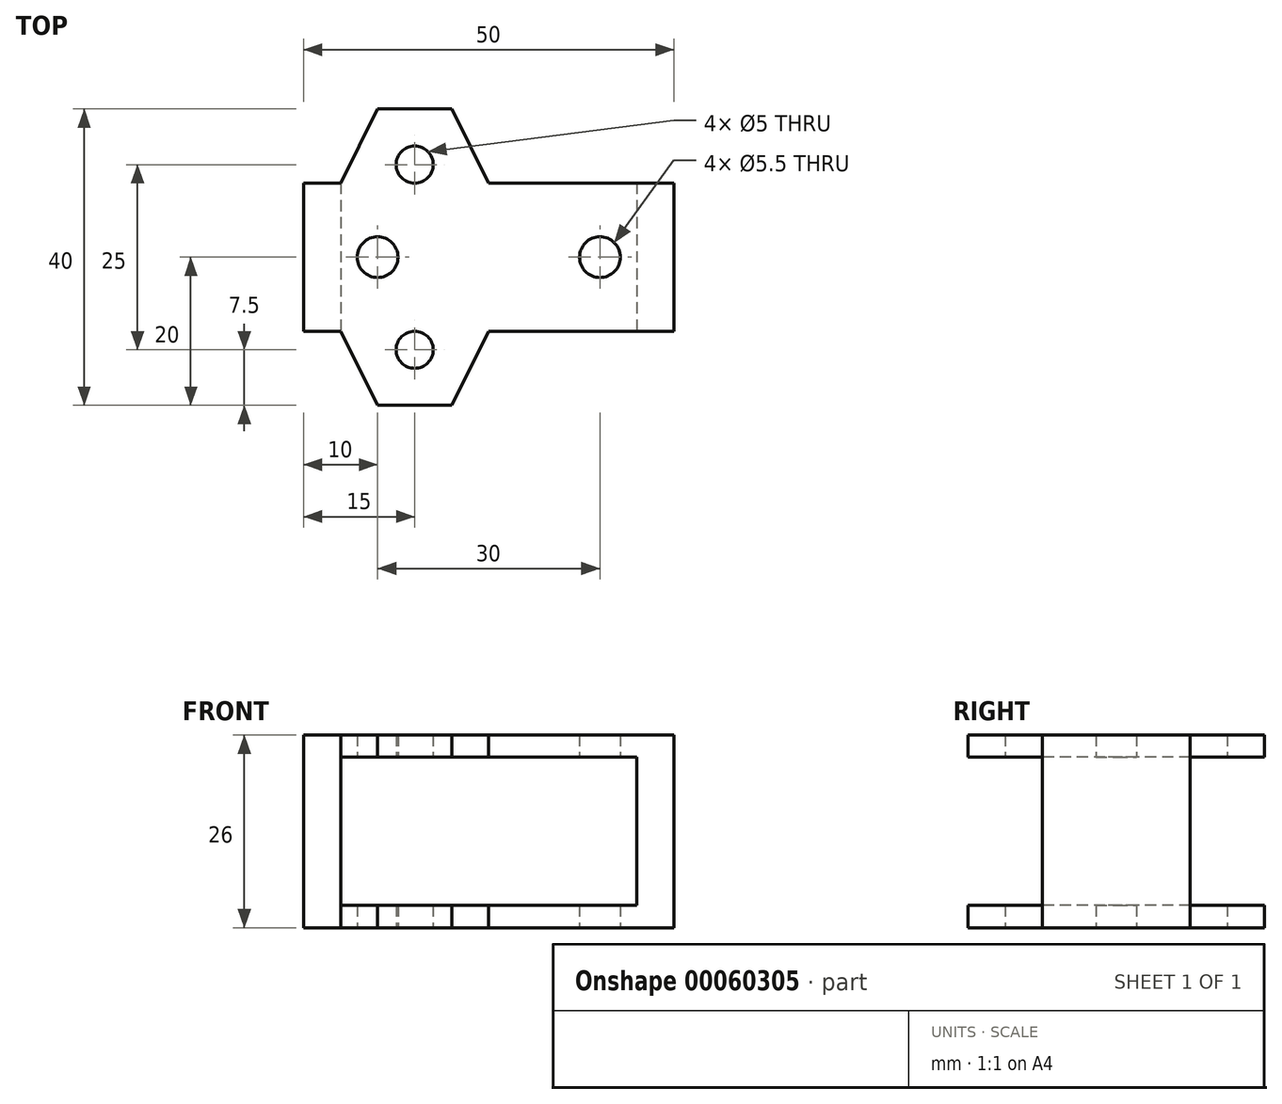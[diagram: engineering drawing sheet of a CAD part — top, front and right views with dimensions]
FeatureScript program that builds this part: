
annotation { "Feature Type Name" : "Feature", "Feature Type Description" : "" }
export const myFeature = defineFeature(function(context is Context, id is Id, definition is map)
    precondition{}
    {
        {
            var Q0;
            Q0=qCreatedBy(makeId("Top.planeOp"),FACE);
            var sketch = newSketch(context, id + "F0", { "sketchPlane" : qUnion([Q0])});
            skLineSegment(sketch, "E0.bottom", {"start": v(-10, 10) * mm, "end": v(10, 10) * mm});
            skLineSegment(sketch, "E0.top", {"start": v(-10, -10) * mm, "end": v(10, -10) * mm});
            skLineSegment(sketch, "E0.left", {"start": v(-10, 10) * mm, "end": v(-10, -10) * mm});
            skLineSegment(sketch, "E0.right", {"start": v(10, 10) * mm, "end": v(10, -10) * mm});
            skLineSegment(sketch, "E1", {"start": v(0, 10) * mm, "end": v(0, -10) * mm, "construction": true});
            skLineSegment(sketch, "E2", {"start": v(-5, 20) * mm, "end": v(5, 20) * mm});
            skLineSegment(sketch, "E3", {"start": v(-5, -20) * mm, "end": v(5, -20) * mm});
            skLineSegment(sketch, "E4", {"start": v(-5, -20) * mm, "end": v(-10, -10) * mm});
            skLineSegment(sketch, "E5", {"start": v(5, -20) * mm, "end": v(10, -10) * mm});
            skLineSegment(sketch, "E6", {"start": v(10, 10) * mm, "end": v(5, 20) * mm});
            skLineSegment(sketch, "E7", {"start": v(-5, 20) * mm, "end": v(-10, 10) * mm});
            skLineSegment(sketch, "E8", {"start": v(0, -10) * mm, "end": v(0, -20) * mm, "construction": true});
            skCircle(sketch, "E9", {"center": v(0, -12.5) * mm, "radius": 2.5 * mm});
            skLineSegment(sketch, "E10.bottom", {"start": v(-10, 10) * mm, "end": v(-15, 10) * mm});
            skLineSegment(sketch, "E10.top", {"start": v(-10, -10) * mm, "end": v(-15, -10) * mm});
            skLineSegment(sketch, "E10.right", {"start": v(-15, 10) * mm, "end": v(-15, -10) * mm});
            skLineSegment(sketch, "E11.bottom", {"start": v(10, 10) * mm, "end": v(30, 10) * mm});
            skLineSegment(sketch, "E11.top", {"start": v(10, -10) * mm, "end": v(30, -10) * mm});
            skLineSegment(sketch, "E11.right", {"start": v(30, 10) * mm, "end": v(30, -10) * mm});
            skLineSegment(sketch, "E12", {"start": v(-5, 10) * mm, "end": v(-5, -10) * mm, "construction": true});
            skLineSegment(sketch, "E13", {"start": v(5, 10) * mm, "end": v(5, -10) * mm, "construction": true});
            skCircle(sketch, "E14", {"center": v(-5, 0) * mm, "radius": 2.75 * mm});
            skCircle(sketch, "E15", {"center": v(25, 0) * mm, "radius": 2.75 * mm});
            skLineSegment(sketch, "E16", {"start": v(0, 10) * mm, "end": v(0, 20) * mm, "construction": true});
            skCircle(sketch, "E17", {"center": v(0, 12.5) * mm, "radius": 2.5 * mm});
            skLineSegment(sketch, "E18.bottom", {"start": v(30, 10) * mm, "end": v(35, 10) * mm});
            skLineSegment(sketch, "E18.top", {"start": v(30, -10) * mm, "end": v(35, -10) * mm});
            skLineSegment(sketch, "E18.right", {"start": v(35, 10) * mm, "end": v(35, -10) * mm});
            skLineSegment(sketch, "E19", {"start": v(25, 10) * mm, "end": v(25, -10) * mm, "construction": true});
            skSolve(sketch);
        }
        {
            var Q0;
            {var subQ3=sQuery(id+"F0.wireOp",EDGE,"E0.left");Q0=makeQuery(id+"F0.imprint","IMPRINT",FACE,{"disambiguationData":[TD([[makeQuery(id+"F0.imprint","IMPRINT",EDGE,{"derivedFrom":subQ3}),1.0]])]});}
            var Q1;
            Q1=makeQuery(id+"F0.imprint","IMPRINT",FACE,{"disambiguationData":[TD([[makeQuery(id+"F0.imprint","IMPRINT",EDGE,{"derivedFrom":sQuery(id+"F0.wireOp",EDGE,"E3")}),1.0]])]});
            var Q2;
            Q2=makeQuery(id+"F0.imprint","IMPRINT",FACE,{"disambiguationData":[TD([[makeQuery(id+"F0.imprint","IMPRINT",EDGE,{"derivedFrom":sQuery(id+"F0.wireOp",EDGE,"E2")}),-1.0]])]});
            var Q3;
            Q3=makeQuery(id+"F0.imprint","IMPRINT",FACE,{"disambiguationData":[TD([[makeQuery(id+"F0.imprint","IMPRINT",EDGE,{"derivedFrom":sQuery(id+"F0.wireOp",EDGE,"E11.bottom")}),-1.0]])]});
            extrude(context, id + "F1", {"entities" : qUnion([Q0, Q1, Q2, Q3]), "depth" : 3 * mm});
        }
        {
            var Q0;
            Q0=makeQuery(id+"F0.imprint","IMPRINT",FACE,{"disambiguationData":[TD([[makeQuery(id+"F0.imprint","IMPRINT",EDGE,{"derivedFrom":sQuery(id+"F0.wireOp",EDGE,"E10.bottom")}),1.0]])]});
            var Q1;
            Q1=makeQuery(id+"F0.imprint","IMPRINT",FACE,{"disambiguationData":[TD([[makeQuery(id+"F0.imprint","IMPRINT",EDGE,{"derivedFrom":sQuery(id+"F0.wireOp",EDGE,"E18.bottom")}),-1.0]])]});
            extrude(context, id + "F2", {"entities" : qUnion([Q0, Q1]), "operationType" : NewBodyOperationType.ADD, "depth" : 26 * mm});
        }
        {
            var Q0;
            Q0=makeQuery(id+"F1.opExtrude","CAP_FACE",FACE,{"disambiguationData":[OSD([sQuery(id+"F0.wireOp",EDGE,"E2"),sQuery(id+"F0.wireOp",EDGE,"E3"),sQuery(id+"F0.wireOp",EDGE,"E4"),sQuery(id+"F0.wireOp",EDGE,"E5"),sQuery(id+"F0.wireOp",EDGE,"E6"),sQuery(id+"F0.wireOp",EDGE,"E7"),sQuery(id+"F0.wireOp",EDGE,"E9"),sQuery(id+"F0.wireOp",EDGE,"E0.left"),sQuery(id+"F0.wireOp",EDGE,"E0.right"),sQuery(id+"F0.wireOp",EDGE,"E14"),sQuery(id+"F0.wireOp",EDGE,"E15"),sQuery(id+"F0.wireOp",EDGE,"E17")])],"isStart":false});
            extrude(context, id + "F3", {"entities" : qUnion([Q0]), "operationType" : NewBodyOperationType.ADD, "depth" : 23 * mm, "hasSecondDirection" : true, "secondDirectionOppositeDirection" : false, "secondDirectionDepth" : 20 * mm});
        }
    });
